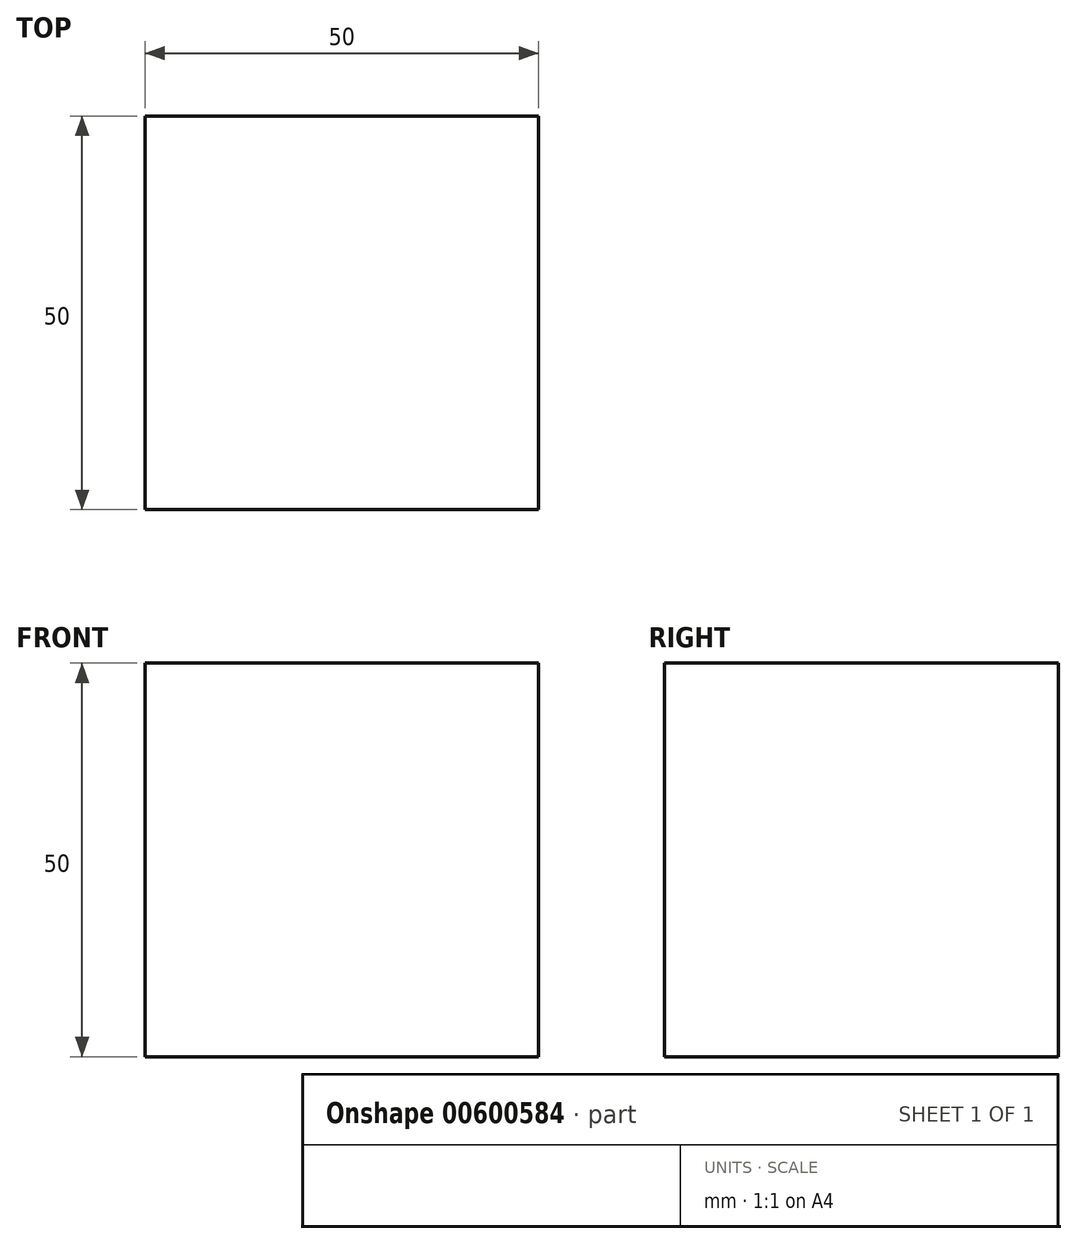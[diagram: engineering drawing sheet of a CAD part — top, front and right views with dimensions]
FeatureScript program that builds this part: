
annotation { "Feature Type Name" : "Feature", "Feature Type Description" : "" }
export const myFeature = defineFeature(function(context is Context, id is Id, definition is map)
    precondition{}
    {
        {
            var Q0;
            Q0=qCreatedBy(makeId("Top.planeOp"),FACE);
            var sketch = newSketch(context, id + "F0", { "sketchPlane" : qUnion([Q0])});
            skLineSegment(sketch, "E0.bottom", {"start": v(-33.55, 32.05) * mm, "end": v(16.45, 32.05) * mm});
            skLineSegment(sketch, "E0.top", {"start": v(-33.55, -17.95) * mm, "end": v(16.45, -17.95) * mm});
            skLineSegment(sketch, "E0.left", {"start": v(-33.55, 32.05) * mm, "end": v(-33.55, -17.95) * mm});
            skLineSegment(sketch, "E0.right", {"start": v(16.45, 32.05) * mm, "end": v(16.45, -17.95) * mm});
            skSolve(sketch);
        }
        {
            var Q0;
            Q0 = qSketchRegion(id + "F0", true);
            extrude(context, id + "F1", {"entities" : qUnion([Q0]), "depth" : 50 * mm, "offsetDistance" : 25 * mm});
        }
    });
